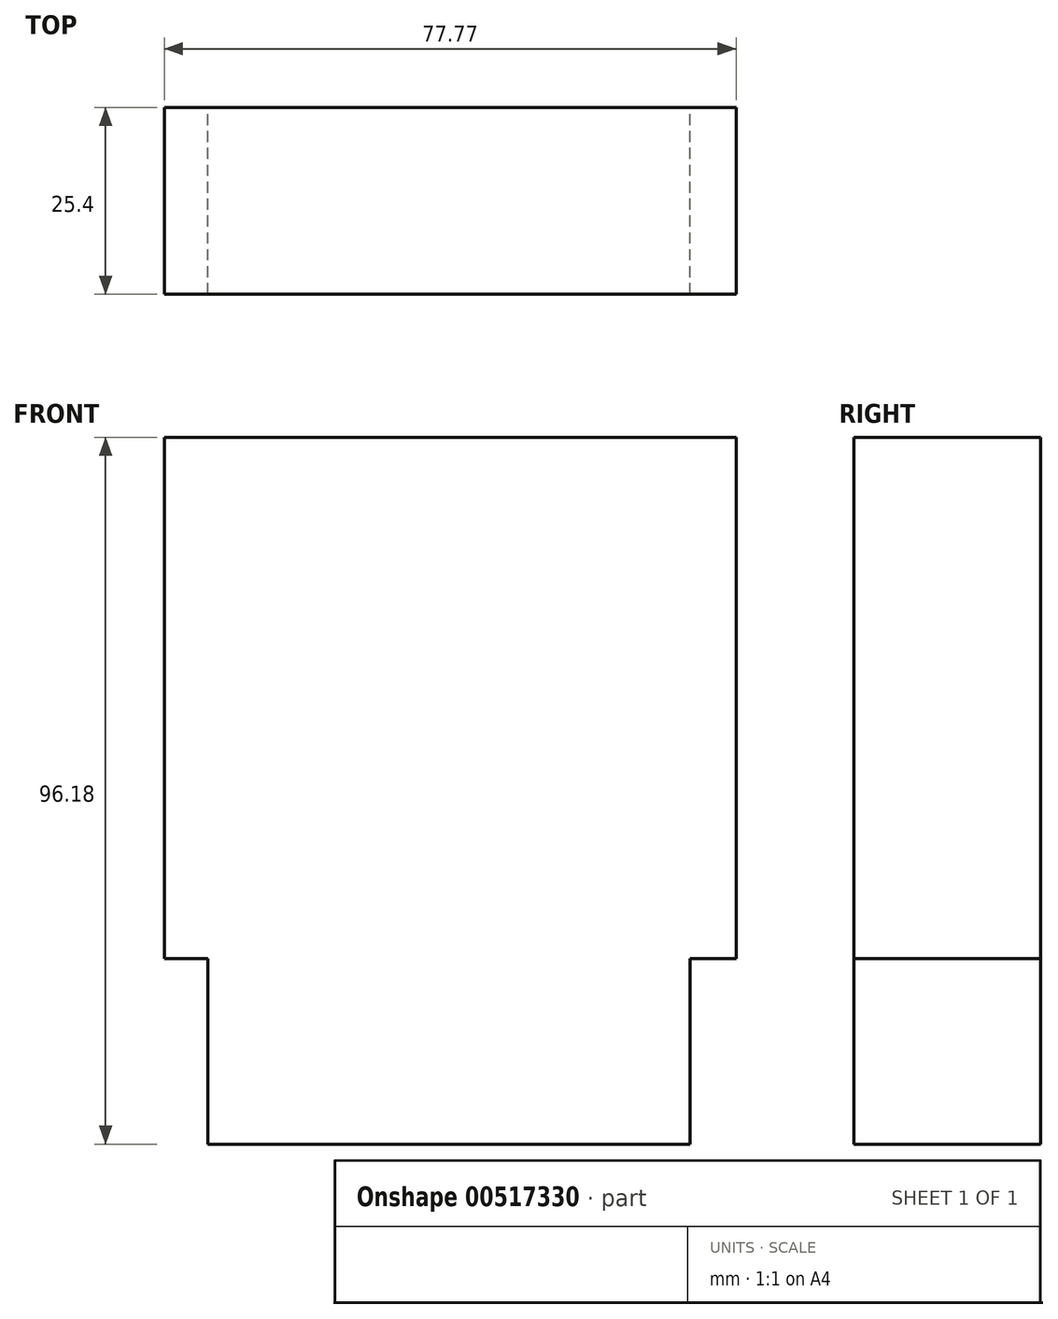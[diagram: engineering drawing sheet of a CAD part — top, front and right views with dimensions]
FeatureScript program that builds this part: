
annotation { "Feature Type Name" : "Feature", "Feature Type Description" : "" }
export const myFeature = defineFeature(function(context is Context, id is Id, definition is map)
    precondition{}
    {
        {
            var Q0;
            Q0=qCreatedBy(makeId("Front.planeOp"),FACE);
            var sketch = newSketch(context, id + "F0", { "sketchPlane" : qUnion([Q0])});
            skLineSegment(sketch, "E0", {"start": v(-48.68, 39.04) * mm, "end": v(-48.68, -25.98) * mm});
            skLineSegment(sketch, "E1", {"start": v(-48.68, -25.98) * mm, "end": v(-42.75, -25.98) * mm});
            skLineSegment(sketch, "E2", {"start": v(-42.75, -25.98) * mm, "end": v(-42.75, -51.2) * mm});
            skLineSegment(sketch, "E3", {"start": v(-42.75, -51.2) * mm, "end": v(22.86, -51.2) * mm});
            skLineSegment(sketch, "E4", {"start": v(22.86, -51.2) * mm, "end": v(22.86, -25.98) * mm});
            skLineSegment(sketch, "E5", {"start": v(22.86, -25.98) * mm, "end": v(29.1, -25.98) * mm});
            skLineSegment(sketch, "E6", {"start": v(29.1, -25.98) * mm, "end": v(29.1, 44.97) * mm});
            skLineSegment(sketch, "E7", {"start": v(29.1, 44.97) * mm, "end": v(-48.68, 44.97) * mm});
            skLineSegment(sketch, "E8", {"start": v(-48.68, 44.97) * mm, "end": v(-48.68, 39.04) * mm});
            skLineSegment(sketch, "E9", {"start": v(-48.68, 39.04) * mm, "end": v(-48.68, 44.97) * mm});
            skSolve(sketch);
        }
        {
            var Q0;
            Q0 = qSketchRegion(id + "F0", true);
            extrude(context, id + "F1", {"entities" : qUnion([Q0]), "depth" : 25.4 * mm, "offsetDistance" : 25.4 * mm});
        }
    });
